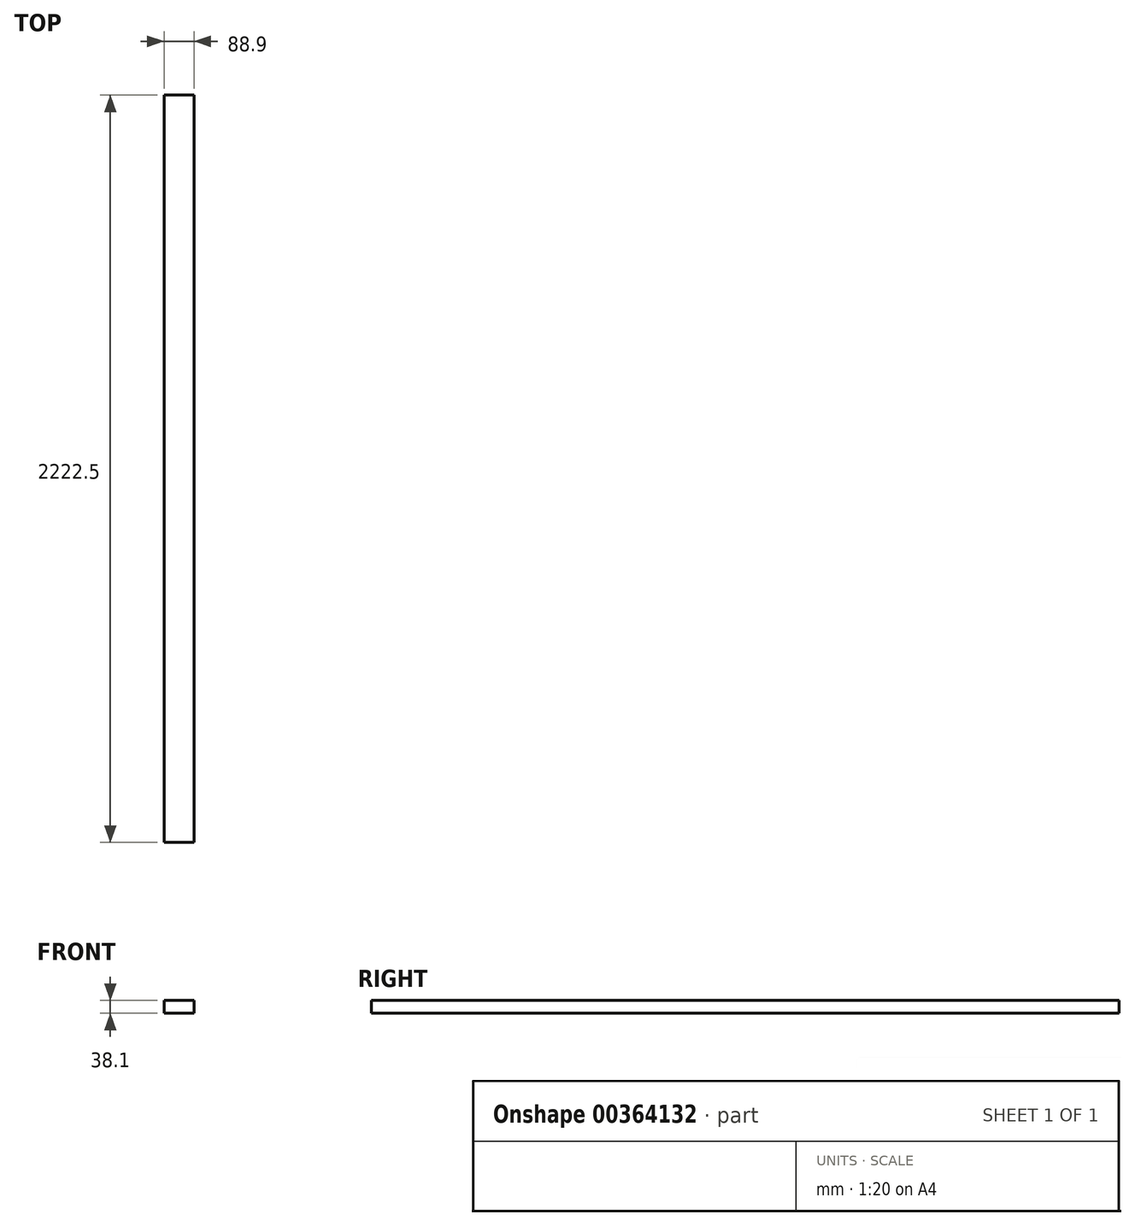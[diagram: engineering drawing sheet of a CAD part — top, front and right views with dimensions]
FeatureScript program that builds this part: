
annotation { "Feature Type Name" : "Feature", "Feature Type Description" : "" }
export const myFeature = defineFeature(function(context is Context, id is Id, definition is map)
    precondition{}
    {
        {
            var Q0;
            Q0=qCreatedBy(makeId("Front.planeOp"),FACE);
            var sketch = newSketch(context, id + "F0", { "sketchPlane" : qUnion([Q0])});
            skLineSegment(sketch, "E0.bottom", {"start": v(-27.05, 30.42) * mm, "end": v(61.85, 30.42) * mm});
            skLineSegment(sketch, "E0.top", {"start": v(-27.05, -7.68) * mm, "end": v(61.85, -7.68) * mm});
            skLineSegment(sketch, "E0.left", {"start": v(-27.05, 30.42) * mm, "end": v(-27.05, -7.68) * mm});
            skLineSegment(sketch, "E0.right", {"start": v(61.85, 30.42) * mm, "end": v(61.85, -7.68) * mm});
            skSolve(sketch);
        }
        {
            var Q0;
            Q0=makeQuery(id+"F0.imprint","IMPRINT",FACE,{"disambiguationData":[TD([[makeQuery(id+"F0.imprint","IMPRINT",EDGE,{"derivedFrom":sQuery(id+"F0.wireOp",EDGE,"E0.bottom")}),-1.0]])]});
            extrude(context, id + "F1", {"entities" : qUnion([Q0]), "depth" : 2222.5 * mm});
        }
    });
